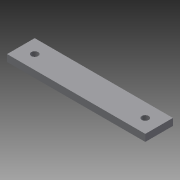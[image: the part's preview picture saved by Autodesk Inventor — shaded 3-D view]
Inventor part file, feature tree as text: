
AUTODESK INVENTOR PART (.ipt)
format: ipt  version: 2013 (Build 170138000, 138)  size: 81,920 bytes
history: native  units: in
note: dims shown in document units (in); Inventor stores cm internally (conversion verified against a paired STEP export)
features: extrude x2, sketch x2
ambient origin geometry x8: Origin, YZ Plane, XZ Plane, XY Plane, X Axis, Y Axis, Z Axis, Center Point
bodies: Solid1 (feature_tree)
feature tree (4):
  extrude  "Extrusion1"  Depth=1.0in
  extrude  "Extrusion2"  Depth=0.5in
  sketch  "Sketch1"  dims[d0=5.0in d1=1.0in]
  sketch  "Sketch2"  dims[d2=0.25in d3=0.0in d4=0.5in d5=0.0in d6=0.5in d7=180.0deg d8=0.25in d9=0.25in d10=0.25in d11=0.0in]
